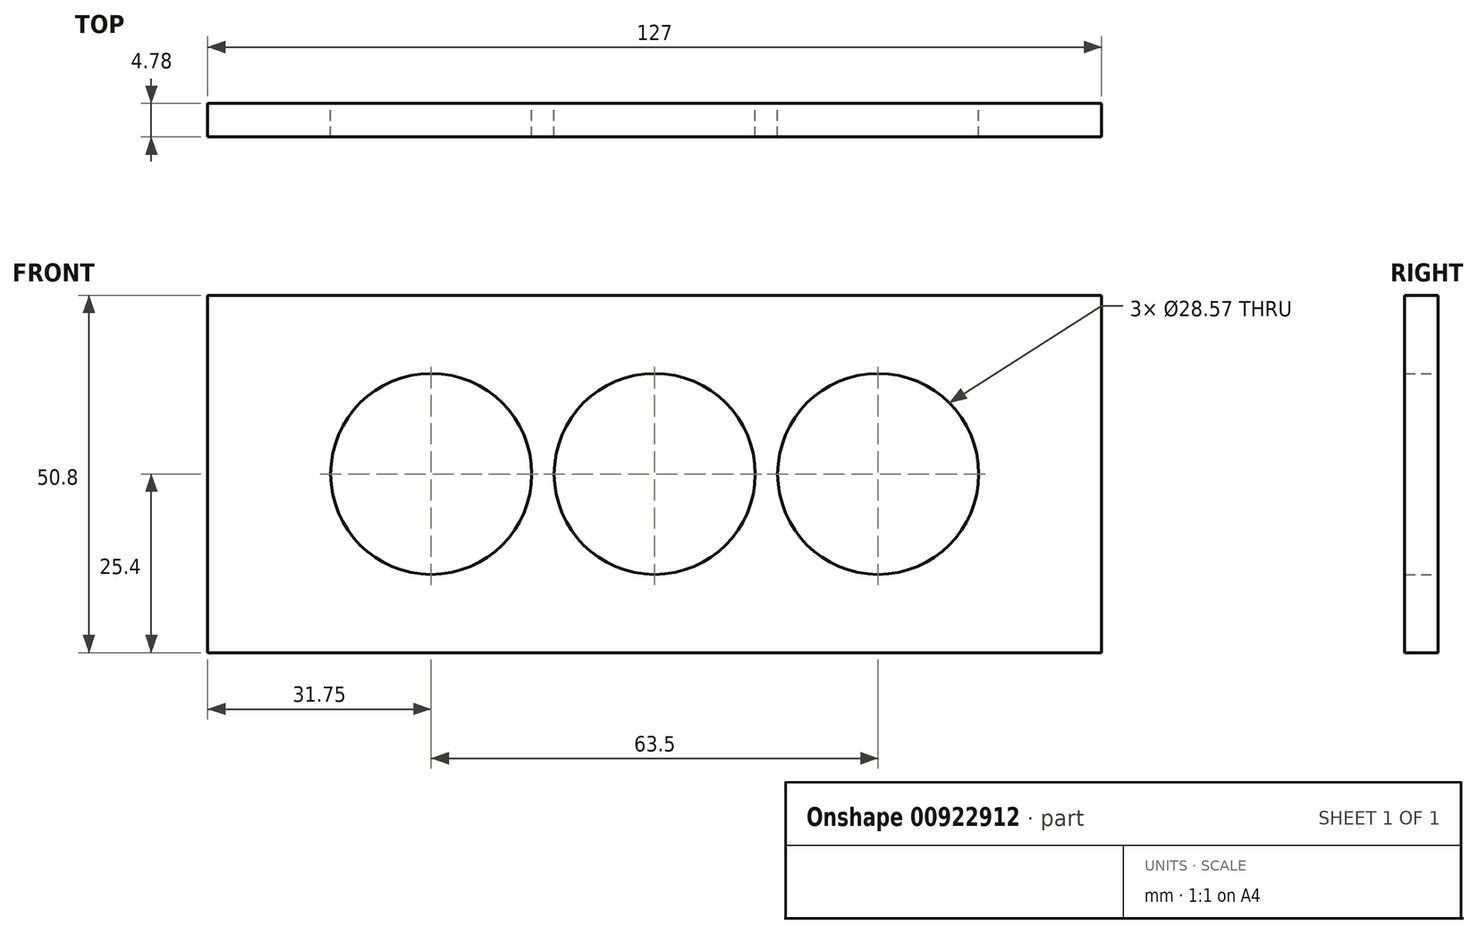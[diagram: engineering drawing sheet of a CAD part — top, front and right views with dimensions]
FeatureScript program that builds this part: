
annotation { "Feature Type Name" : "Feature", "Feature Type Description" : "" }
export const myFeature = defineFeature(function(context is Context, id is Id, definition is map)
    precondition{}
    {
        {
            var Q0;
            Q0=qCreatedBy(makeId("Front.planeOp"),FACE);
            var sketch = newSketch(context, id + "F0", { "sketchPlane" : qUnion([Q0])});
            skLineSegment(sketch, "E0.bottom", {"start": v(63.5, -25.4) * mm, "end": v(-63.5, -25.4) * mm});
            skLineSegment(sketch, "E0.top", {"start": v(63.5, 25.4) * mm, "end": v(-63.5, 25.4) * mm});
            skLineSegment(sketch, "E0.left", {"start": v(63.5, -25.4) * mm, "end": v(63.5, 25.4) * mm});
            skLineSegment(sketch, "E0.right", {"start": v(-63.5, -25.4) * mm, "end": v(-63.5, 25.4) * mm});
            skPoint(sketch, "E0.middle", {"position": v(0, 0) * mm});
            skCircle(sketch, "E1", {"center": v(0, 0) * mm, "radius": 14.29 * mm});
            skCircle(sketch, "E2", {"center": v(-31.75, 0) * mm, "radius": 14.29 * mm});
            skCircle(sketch, "E3", {"center": v(31.75, 0) * mm, "radius": 14.29 * mm});
            skSolve(sketch);
        }
        {
            var Q0;
            Q0=makeQuery(id+"F0.imprint","IMPRINT",FACE,{"disambiguationData":[TD([[makeQuery(id+"F0.imprint","IMPRINT",EDGE,{"derivedFrom":sQuery(id+"F0.wireOp",EDGE,"E0.bottom")}),-1.0]])]});
            extrude(context, id + "F1", {"entities" : qUnion([Q0]), "depth" : 4.78 * mm, "offsetDistance" : 25.4 * mm});
        }
    });
